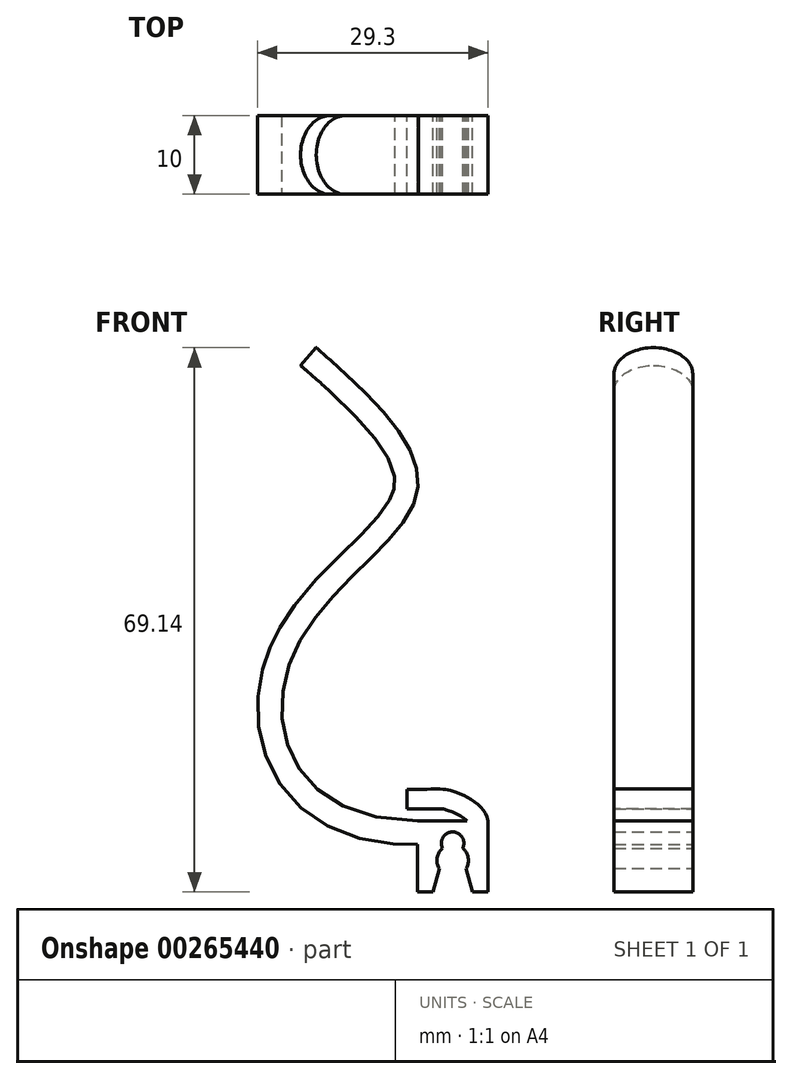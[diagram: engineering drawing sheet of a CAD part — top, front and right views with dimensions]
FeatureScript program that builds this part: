
annotation { "Feature Type Name" : "Feature", "Feature Type Description" : "" }
export const myFeature = defineFeature(function(context is Context, id is Id, definition is map)
    precondition{}
    {
        {
            var Q0;
            Q0=qCreatedBy(makeId("Front.planeOp"),FACE);
            var sketch = newSketch(context, id + "F0", { "sketchPlane" : qUnion([Q0])});
            skFitSpline(sketch, "E0", {"points": [v(-12.84, 60.1) * mm, v(0, 41.65) * mm, v(-15.88, 20.88) * mm, v(0, 0) * mm], "startDerivative": vector(66.8, -58.63) * mm, "endDerivative": vector(140.52, 0) * mm});
            skFitSpline(sketch, "E1.0", {"points": [v(-14.81, 57.84) * mm, v(-13.43, 56.62) * mm, v(-10.7, 54.2) * mm, v(-7.67, 51.23) * mm, v(-5.7, 48.96) * mm, v(-4.5, 47.34) * mm, v(-3.6, 45.83) * mm, v(-3.06, 44.48) * mm, v(-2.87, 43.52) * mm, v(-2.85, 42.85) * mm, v(-2.9, 42.46) * mm, v(-2.96, 42.15) * mm, v(-3.05, 41.82) * mm, v(-3.22, 41.37) * mm, v(-3.52, 40.77) * mm, v(-4.05, 39.9) * mm, v(-4.96, 38.7) * mm, v(-6.4, 37.11) * mm, v(-8.07, 35.42) * mm, v(-10.52, 33.02) * mm, v(-13.13, 30.37) * mm, v(-15.58, 27.38) * mm, v(-16.97, 25.34) * mm, v(-17.95, 23.58) * mm, v(-18.6, 22.2) * mm, v(-19.15, 20.76) * mm, v(-19.74, 18.8) * mm, v(-20.2, 16.26) * mm, v(-20.26, 13.16) * mm, v(-19.81, 10.07) * mm, v(-18.8, 7.07) * mm, v(-17.17, 4.26) * mm, v(-14.92, 1.77) * mm, v(-12.05, -0.3) * mm, v(-8.6, -1.83) * mm, v(-4.62, -2.78) * mm, v(-1.6, -3) * mm, v(0, -3) * mm]});
            skLineSegment(sketch, "E2", {"start": v(-12.84, 60.1) * mm, "end": v(-14.81, 57.84) * mm});
            skLineSegment(sketch, "E3", {"start": v(0, -3) * mm, "end": v(0, -9.05) * mm});
            skLineSegment(sketch, "E4", {"start": v(0, -9.05) * mm, "end": v(2, -9.05) * mm});
            skLineSegment(sketch, "E5", {"start": v(9, -9.05) * mm, "end": v(9, 0) * mm});
            skLineSegment(sketch, "E6", {"start": v(9, 0) * mm, "end": v(0, 0) * mm});
            skArc(sketch, "E7", {"start": v(3.21, -3.49) * mm, "mid": v(2.53, -4.7) * mm, "end": v(2.8, -6.07) * mm});
            skPoint(sketch, "E7.centerSnap0", {"position": v(4.5, 0) * mm});
            skArc(sketch, "E8", {"start": v(5.79, -3.49) * mm, "mid": v(4.5, -1.43) * mm, "end": v(3.21, -3.49) * mm});
            skLineSegment(sketch, "E9", {"start": v(2, -9.05) * mm, "end": v(2.8, -6.07) * mm});
            skLineSegment(sketch, "E10.trimOffspring", {"start": v(6.2, -6.07) * mm, "end": v(7, -9.05) * mm});
            skArc(sketch, "E11.trimOffspring", {"start": v(6.2, -6.07) * mm, "mid": v(6.47, -4.7) * mm, "end": v(5.79, -3.49) * mm});
            skPoint(sketch, "E12.1.internal.snap0", {"position": v(4.5, -1.43) * mm});
            skFitSpline(sketch, "E12", {"points": [v(9, 0) * mm, v(4.5, 3.75) * mm, v(0, 4) * mm], "startDerivative": vector(-1.62, 11.28) * mm, "endDerivative": vector(-16.5, 0.07) * mm});
            skFitSpline(sketch, "E13.0", {"points": [v(6.53, -0.36) * mm, v(6.53, -0.35) * mm, v(6.53, -0.34) * mm, v(6.45, -0.2) * mm, v(6.25, 0.04) * mm, v(5.92, 0.32) * mm, v(5.48, 0.61) * mm, v(4.98, 0.88) * mm, v(4.47, 1.1) * mm, v(4.06, 1.26) * mm, v(3.77, 1.36) * mm, v(3.52, 1.43) * mm, v(3.3, 1.48) * mm, v(3.07, 1.51) * mm, v(2.78, 1.53) * mm, v(2.36, 1.53) * mm, v(1.57, 1.51) * mm, v(0.7, 1.5) * mm, v(-0.01, 1.5) * mm]});
            skLineSegment(sketch, "E14", {"start": v(3.13, 1.5) * mm, "end": v(0, 1.5) * mm});
            skLineSegment(sketch, "E15.bottom", {"start": v(0, 4) * mm, "end": v(-1.28, 4) * mm});
            skLineSegment(sketch, "E15.top", {"start": v(0, 1.5) * mm, "end": v(-1.28, 1.5) * mm});
            skLineSegment(sketch, "E15.left", {"start": v(0, 4) * mm, "end": v(0, 1.5) * mm});
            skLineSegment(sketch, "E15.right", {"start": v(-1.28, 4) * mm, "end": v(-1.28, 1.5) * mm});
            skLineSegment(sketch, "E16.trimOffspring", {"start": v(7, -9.05) * mm, "end": v(9, -9.05) * mm});
            skSolve(sketch);
        }
        {
            var Q0;
            Q0 = qSketchRegion(id + "F0", true);
            extrude(context, id + "F1", {"entities" : qUnion([Q0]), "depth" : 10 * mm});
        }
        {
            var Q0;
            Q0=makeQuery(id+"F1.opExtrude","CAP_EDGE",EDGE,{"disambiguationData":[OSD([sQuery(id+"F0.wireOp",EDGE,"E2")])],"isStart":false});
            var Q1;
            Q1=makeQuery(id+"F1.opExtrude","CAP_EDGE",EDGE,{"disambiguationData":[OSD([sQuery(id+"F0.wireOp",EDGE,"E2")])],"isStart":true});
            fillet(context, id + "F2", {"entities" : qUnion([Q0, Q1]), "radius" : 5 * mm, "tangentPropagation" : true, "allowEdgeOverflow" : false});
        }
    });
